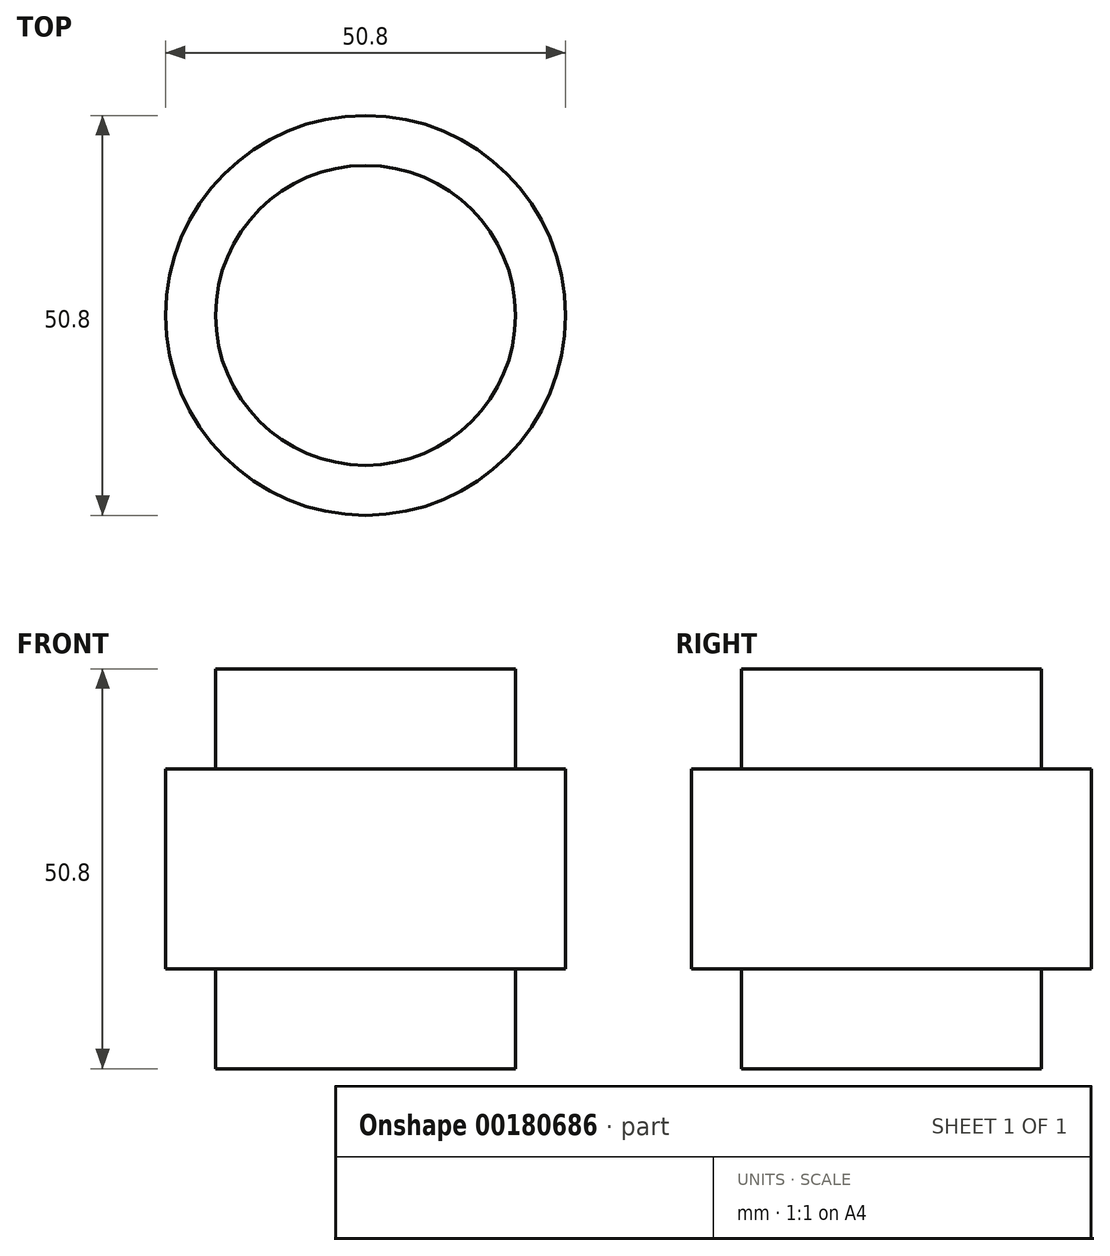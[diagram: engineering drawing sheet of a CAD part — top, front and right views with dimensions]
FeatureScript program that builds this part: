
annotation { "Feature Type Name" : "Feature", "Feature Type Description" : "" }
export const myFeature = defineFeature(function(context is Context, id is Id, definition is map)
    precondition{}
    {
        {
            var Q0;
            Q0=qCreatedBy(makeId("Top.planeOp"),FACE);
            var sketch = newSketch(context, id + "F0", { "sketchPlane" : qUnion([Q0])});
            skCircle(sketch, "E0", {"center": v(0, 0) * mm, "radius": 25.4 * mm});
            skCircle(sketch, "E1", {"center": v(0, 0) * mm, "radius": 19.05 * mm});
            skSolve(sketch);
        }
        {
            var Q0;
            Q0=makeQuery(id+"F0.imprint","IMPRINT",FACE,{"disambiguationData":[TD([[makeQuery(id+"F0.imprint","IMPRINT",EDGE,{"derivedFrom":sQuery(id+"F0.wireOp",EDGE,"E1")}),1.0]])]});
            extrude(context, id + "F1", {"entities" : qUnion([Q0]), "endBound" : BoundingType.SYMMETRIC, "depth" : 50.8 * mm});
        }
        {
            var Q0;
            Q0=qSketchRegion(id+"F0",true);
            extrude(context, id + "F2", {"entities" : qUnion([Q0]), "operationType" : NewBodyOperationType.ADD, "endBound" : BoundingType.SYMMETRIC, "depth" : 25.4 * mm});
        }
    });
